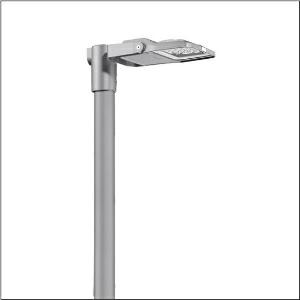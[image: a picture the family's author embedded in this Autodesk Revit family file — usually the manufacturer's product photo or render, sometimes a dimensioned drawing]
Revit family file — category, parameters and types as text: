
# Revit family: floodlight_fl_21_iq_micro___pl52_5xa7762a2d3a_f78f
name_source: partatom
category: Lighting Fixtures
units: mm (PartAtom-declared; Revit-internal decimal feet)

## family parameters
Cut with Voids When Loaded = No
Host = Face
Light Source = No
Part Type = Normal
Room Calculation Point = No
Round Connector Dimension = Use Diameter
Shared = No

## types (1)
- --- (1 x LED, 2890 lm, 23.1 W, 3000K)
    Apparent Load = 23 VA
    CIE Flux Codes = 26 60 98 100 100
    Color Rendering = 70
    Color Temperature = 3000K
    Default Elevation = 1800 mm
    Description = Floodlight FL 21 iQ micro, floodlight, primary light control with lens, of PMMA, primary optical cover: protective disc, of toughened safety glass, transparent, light distribution: PL52, light emission: direct distribution, installation type: surface-mounted, LED, High Power LED, rated luminous flux: 2.890lm, luminous efficacy: 125lm/W, light colour: 730, colour temperature: 3000K, control: Auto-Match, Temp-Guard, Night-Set, Smart-Wire, Desk-Remote (wireless, voltage-free reading and setting of iQ features in the workshop via application-optimized NFC function/RFID function), optimised constant luminous flux control (CLO 2.0), Street-Remote, with terminal, 6-pole, mains connection: 220..240V, AC, 50/60Hz, start of lifetime: 23W, end of service life: 24W, reduction: 11W, luminaire housing, of diecast aluminium, powder-coated, Siteco® metallic grey (DB 702S), corrosivity category C5 mid according to DIN EN ISO 12944, sealing non-destructively replaceable, please order mast flange separately, mast bracket, of steel, galvanised, powder-coated, Siteco® metallic grey (DB 702S), protection rating (complete): IP66, insulation class (complete): insulation class II (safety insulation), certification: CE, ENEC, VDE, protection symbol: D, impact resistance: IK07, permissible operating ambient temperature: -40..+40°C, permissible operating ambient temperature for outdoor applications: -40..+50°C, standard: DIN EN 12944, LABS conformity tested according to VDMA 24364:2018-05, packaging unit: 1 piece

Light Distribution: PL52
    Height = 65 mm
    Lamp = 1 x LED
    Lamp Light Flux = 2890 lm
    Lamp Power = 23.1 W
    Lamp count = 1
    Length = 312 mm
    Luminous efficacy = 125 lm/W
    Manufacturer = Siteco
    ModVariant = No
    Model = 5XA7762A2D3A
    Number of Poles = 1
    OnlyDefault = Yes
    Power Factor = 1
    Product Name = Floodlight FL 21 iQ micro | PL52
    Product group = floodlight | pylon annexe
    ProductGroupID = 6200
    Protection Class = Protection class II
    Protection Degree = IP 66
    RLX_Detail_Level = 1
    RLX_Emergency_Light_Flux = 0 lm
    RLX_Emergency_Type = 0
    RLX_Emergency_Type_DB = No
    RlxData = <blob elided: 102013 chars, md5=dc47464a>
    Socket = socket
    Standby Power = 0 W
    System Light Flux = 2890 lm
    System Power = 23 W
    Type Comments = factory setting: luminous flux: 100 % | dim-lin: 254 | 455 mA
    Type Image = l_1007121.jpg
    URL = http://relux.com
    VarID = @adj_110633
    Voltage = 0 V
    Weight = 0.00 kg
    Width = 230 mm

## geometry (parser evidence)
native form markers: Blend x4, Sweep x12
no freeform markers — native parametric forms only
